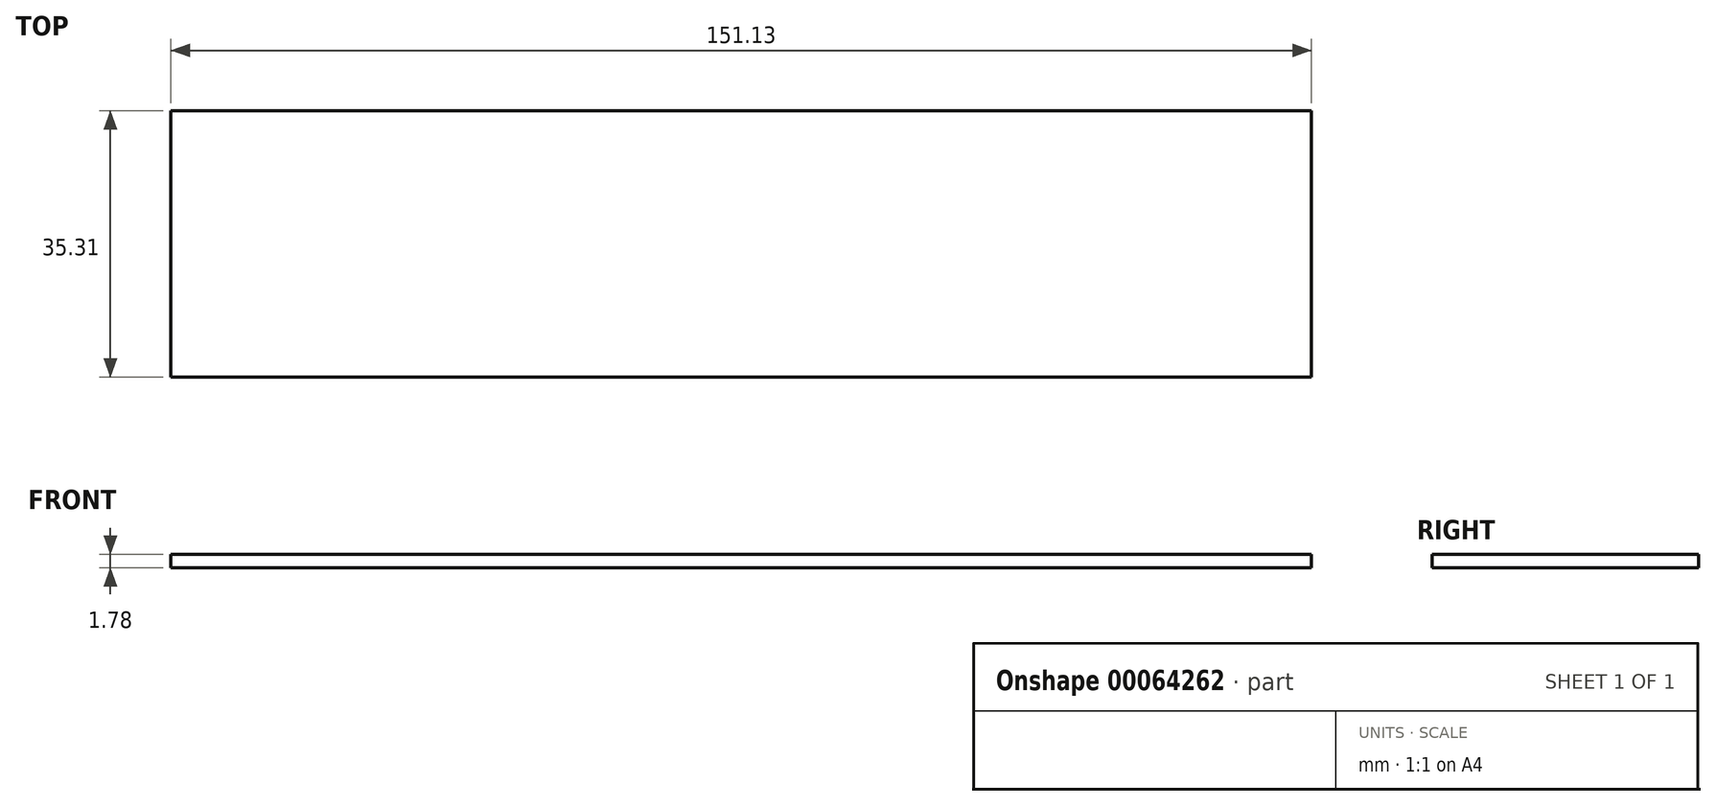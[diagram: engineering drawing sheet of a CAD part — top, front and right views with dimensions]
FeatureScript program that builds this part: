
annotation { "Feature Type Name" : "Feature", "Feature Type Description" : "" }
export const myFeature = defineFeature(function(context is Context, id is Id, definition is map)
    precondition{}
    {
        {
            var Q0;
            Q0=qCreatedBy(makeId("Top.planeOp"),FACE);
            var sketch = newSketch(context, id + "F0", { "sketchPlane" : qUnion([Q0])});
            skLineSegment(sketch, "E0.bottom", {"start": v(-76.39, -103.26) * mm, "end": v(74.74, -103.26) * mm});
            skLineSegment(sketch, "E0.top", {"start": v(-76.39, -138.57) * mm, "end": v(74.74, -138.57) * mm});
            skLineSegment(sketch, "E0.left", {"start": v(-76.39, -103.26) * mm, "end": v(-76.39, -138.57) * mm});
            skLineSegment(sketch, "E0.right", {"start": v(74.74, -103.26) * mm, "end": v(74.74, -138.57) * mm});
            skSolve(sketch);
        }
        {
            var Q0;
            Q0 = qSketchRegion(id + "F0", true);
            extrude(context, id + "F1", {"entities" : qUnion([Q0]), "depth" : 1.78 * mm, "offsetDistance" : 25.4 * mm});
        }
    });
